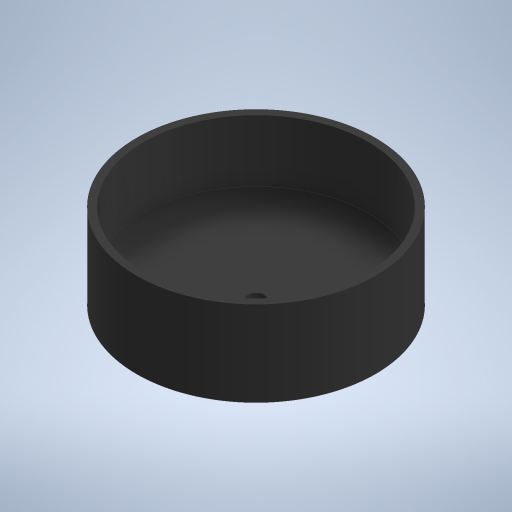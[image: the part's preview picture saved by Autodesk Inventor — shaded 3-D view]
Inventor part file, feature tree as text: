
AUTODESK INVENTOR PART (.ipt)
format: ipt  version: 2024 (Build 280153020, 153B)  size: 241,664 bytes
history: native  units: mm
features: sketch x2, revolve x1, extrude x1
ambient origin geometry x8: Origin, YZ Plane, XZ Plane, XY Plane, X Axis, Y Axis, Z Axis, Center Point
bodies: Solid1 (feature_tree)
feature tree (4):
  revolve  "Revolution1"  [1 undecoded]
  extrude  "Extrusion1"  Depth=25.0mm
  sketch  "Sketch1"  dims[d2=1.5mm d6=29.0mm]
  sketch  "Sketch3"  dims[d8=35.0mm d20=25.0mm d21=2.0mm d22=5.0mm d23=180.0deg d24=180.0deg d25=4.8mm d26=10.0mm d27=0.0mm d15=0.872665mm d16=0.872665mm]
note: 1 required parameter value undecoded (feature->parameter linkage not recoverable at this tier; creation-order binding heuristic only, values carry confidence <= 0.55)
